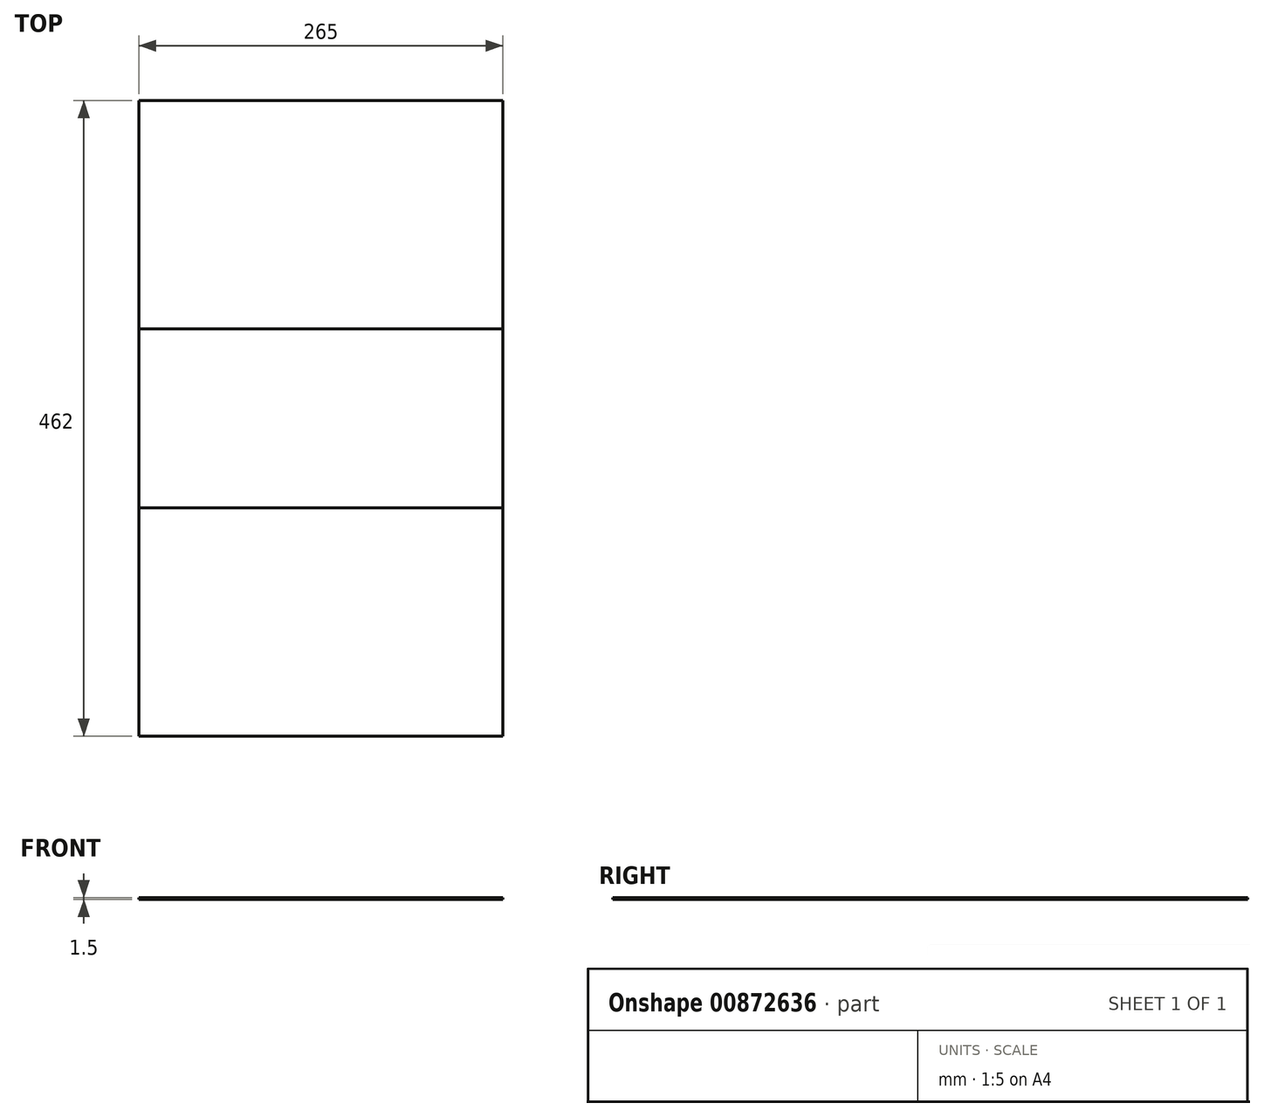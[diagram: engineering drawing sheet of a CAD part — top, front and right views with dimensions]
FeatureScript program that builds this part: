
annotation { "Feature Type Name" : "Feature", "Feature Type Description" : "" }
export const myFeature = defineFeature(function(context is Context, id is Id, definition is map)
    precondition{}
    {
        {
            var Q0;
            Q0=qCreatedBy(makeId("Top.planeOp"),FACE);
            var sketch = newSketch(context, id + "F0", { "sketchPlane" : qUnion([Q0])});
            skLineSegment(sketch, "E0.bottom", {"start": v(-189.26, 80.1) * mm, "end": v(75.74, 80.1) * mm});
            skLineSegment(sketch, "E0.top", {"start": v(-189.26, -85.9) * mm, "end": v(75.74, -85.9) * mm});
            skLineSegment(sketch, "E0.left", {"start": v(-189.26, 80.1) * mm, "end": v(-189.26, -85.9) * mm});
            skLineSegment(sketch, "E0.right", {"start": v(75.74, 80.1) * mm, "end": v(75.74, -85.9) * mm});
            skSolve(sketch);
        }
        {
            var Q0;
            Q0=qCreatedBy(makeId("Top.planeOp"),FACE);
            var sketch = newSketch(context, id + "F1", { "sketchPlane" : qUnion([Q0])});
            skLineSegment(sketch, "E1.bottom", {"start": v(-189.26, -85.9) * mm, "end": v(75.74, -85.9) * mm});
            skLineSegment(sketch, "E1.top", {"start": v(-189.26, -215.9) * mm, "end": v(75.74, -215.9) * mm});
            skLineSegment(sketch, "E1.left", {"start": v(-189.26, -85.9) * mm, "end": v(-189.26, -215.9) * mm});
            skLineSegment(sketch, "E1.right", {"start": v(75.74, -85.9) * mm, "end": v(75.74, -215.9) * mm});
            skSolve(sketch);
        }
        {
            var Q0;
            Q0=qCreatedBy(makeId("Top.planeOp"),FACE);
            var sketch = newSketch(context, id + "F2", { "sketchPlane" : qUnion([Q0])});
            skLineSegment(sketch, "E2.bottom", {"start": v(-189.26, -215.9) * mm, "end": v(75.74, -215.9) * mm});
            skLineSegment(sketch, "E2.top", {"start": v(-189.26, -381.9) * mm, "end": v(75.74, -381.9) * mm});
            skLineSegment(sketch, "E2.left", {"start": v(-189.26, -215.9) * mm, "end": v(-189.26, -381.9) * mm});
            skLineSegment(sketch, "E2.right", {"start": v(75.74, -215.9) * mm, "end": v(75.74, -381.9) * mm});
            skSolve(sketch);
        }
        {
            var Q0;
            Q0=makeQuery(id+"F0.imprint","IMPRINT",FACE,{"disambiguationData":[TD([[makeQuery(id+"F0.imprint","IMPRINT",EDGE,{"derivedFrom":sQuery(id+"F0.wireOp",EDGE,"E0.bottom")}),-1.0]])]});
            var Q1;
            Q1=makeQuery(id+"F1.imprint","IMPRINT",FACE,{"disambiguationData":[TD([[makeQuery(id+"F1.imprint","IMPRINT",EDGE,{"derivedFrom":sQuery(id+"F1.wireOp",EDGE,"E1.bottom")}),-1.0]])]});
            var Q2;
            Q2=makeQuery(id+"F2.imprint","IMPRINT",FACE,{"disambiguationData":[TD([[makeQuery(id+"F2.imprint","IMPRINT",EDGE,{"derivedFrom":sQuery(id+"F2.wireOp",EDGE,"E2.bottom")}),-1.0]])]});
            extrude(context, id + "F3", {"entities" : qUnion([Q0, Q1, Q2]), "depth" : 1.5 * mm, "offsetDistance" : 25 * mm});
        }
    });
